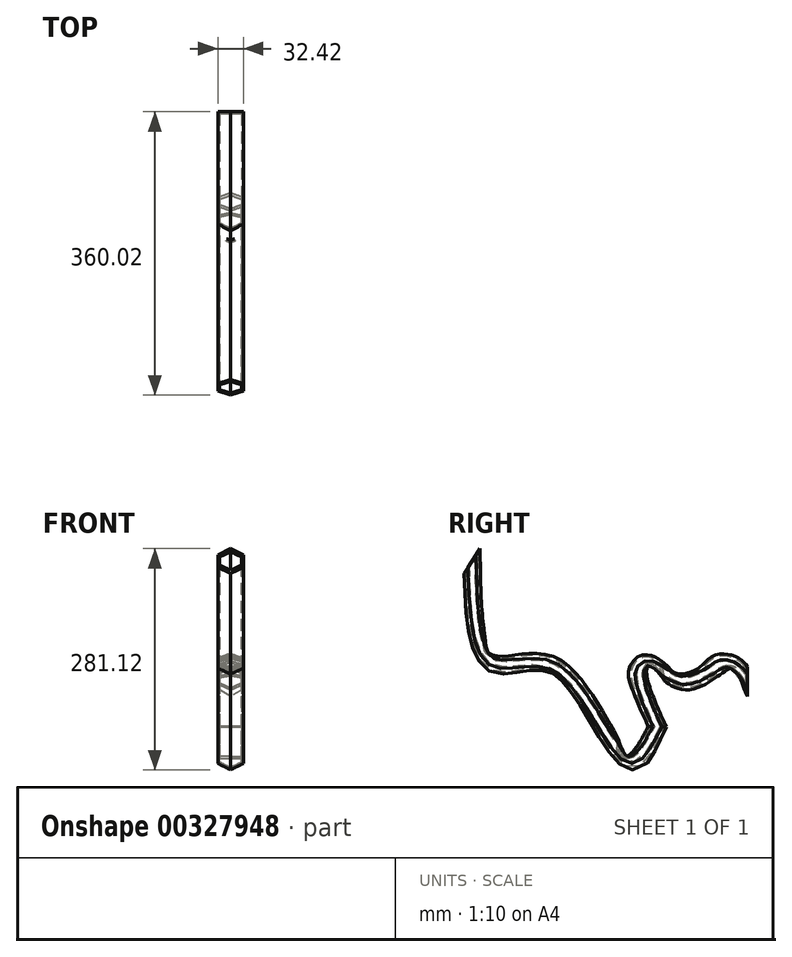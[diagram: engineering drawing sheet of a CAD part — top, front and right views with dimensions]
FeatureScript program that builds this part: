
annotation { "Feature Type Name" : "Feature", "Feature Type Description" : "" }
export const myFeature = defineFeature(function(context is Context, id is Id, definition is map)
    precondition{}
    {
        {
            var Q0;
            Q0=qCreatedBy(makeId("Front.planeOp"),FACE);
            var sketch = newSketch(context, id + "F0", { "sketchPlane" : qUnion([Q0])});
            skCircle(sketch, "E0.cCircle", {"center": v(0, 0) * mm, "radius": 16.21 * mm, "construction": true});
            skLineSegment(sketch, "E0.0", {"start": v(16.21, 9.36) * mm, "end": v(16.21, -9.36) * mm});
            skLineSegment(sketch, "E0.1", {"start": v(16.21, -9.36) * mm, "end": v(0, -18.72) * mm});
            skLineSegment(sketch, "E0.2", {"start": v(0, -18.72) * mm, "end": v(-16.21, -9.36) * mm});
            skLineSegment(sketch, "E0.3", {"start": v(-16.21, -9.36) * mm, "end": v(-16.21, 9.36) * mm});
            skLineSegment(sketch, "E0.4", {"start": v(-16.21, 9.36) * mm, "end": v(0, 18.72) * mm});
            skLineSegment(sketch, "E0.5", {"start": v(0, 18.72) * mm, "end": v(16.21, 9.36) * mm});
            skPoint(sketch, "E0.0.midPoint", {"position": v(16.21, 0) * mm});
            skSolve(sketch);
        }
        {
            var Q0;
            Q0=qCreatedBy(makeId("Right.planeOp"),FACE);
            var sketch = newSketch(context, id + "F1", { "sketchPlane" : qUnion([Q0])});
            skFitSpline(sketch, "E1", {"points": [v(0, 0) * mm, v(-12.67, 15.34) * mm, v(-29.78, 21.78) * mm, v(-46.9, 14.45) * mm, v(-84.23, 2.89) * mm, v(-122.46, 20.22) * mm, v(-135.8, 11.78) * mm, v(-114.8, -57.19) * mm], "startDerivative": vector(-95.26, 143.87) * mm, "endDerivative": vector(166.51, -374.66) * mm});
            skFitSpline(sketch, "E2", {"points": [v(-114.8, -57.19) * mm, v(-152.29, -96.41) * mm, v(-242.8, 16.74) * mm, v(-323.51, 26.14) * mm, v(-350.03, 153.24) * mm], "startDerivative": vector(-189.58, -361.2) * mm, "endDerivative": vector(-13.11, 598.19) * mm});
            skSolve(sketch);
        }
        {
            var Q0;
            Q0=makeQuery(id+"F0.imprint","IMPRINT",FACE,{"disambiguationData":[TD([[makeQuery(id+"F0.imprint","IMPRINT",EDGE,{"derivedFrom":sQuery(id+"F0.wireOp",EDGE,"E0.0")}),-1.0]])]});
            var Q1;
            Q1=sQuery(id+"F1.wireOp",EDGE,"E1");
            var Q2;
            Q2=sQuery(id+"F1.wireOp",EDGE,"E2");
            sweep(context, id + "F2", {"profiles" : qUnion([Q0]), "path" : qUnion([Q1, Q2])});
        }
        {
            var Q0;
            Q0=makeQuery(id+"F2.opSweep","CAP_FACE",FACE,{"disambiguationData":[OSD([sQuery(id+"F0.wireOp",EDGE,"E0.0"),sQuery(id+"F0.wireOp",EDGE,"E0.1"),sQuery(id+"F0.wireOp",EDGE,"E0.2"),sQuery(id+"F0.wireOp",EDGE,"E0.3"),sQuery(id+"F0.wireOp",EDGE,"E0.4"),sQuery(id+"F0.wireOp",EDGE,"E0.5"),sQuery(id+"F1.wireOp",VERTEX,"E2.end")])],"isStart":false});
            shell(context, id + "F3", {"entities" : qUnion([Q0]), "thickness" : 2.54 * mm});
        }
    });
